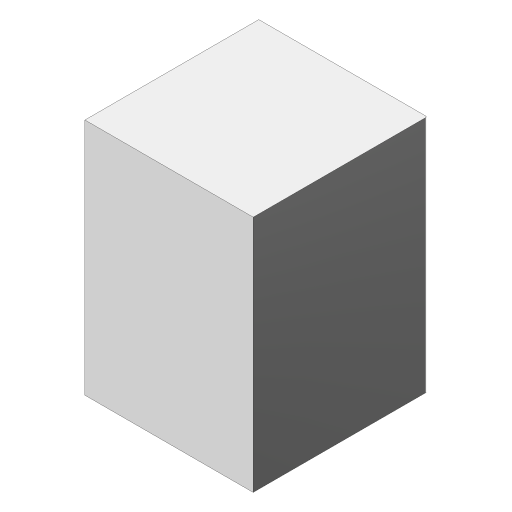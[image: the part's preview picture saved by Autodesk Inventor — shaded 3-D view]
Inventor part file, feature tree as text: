
AUTODESK INVENTOR PART (.ipt)
format: ipt  version: 2023 (Build 270158000, 158)  size: 90,624 bytes
history: native  units: mm
features: extrude x1, fillet x1, sketch x1
ambient origin geometry x8: Origin, YZ Plane, XZ Plane, XY Plane, X Axis, Y Axis, Z Axis, Center Point
bodies: 实体1 (feature_tree)
feature tree (3):
  extrude  "拉伸1"  Depth=620.0mm
  fillet  "圆角1"  Radius=600.0mm
  sketch  "草图1"  dims[d0=850.0mm d1=620.0mm d2=600.0mm d3=0.0mm d4=5.0mm]
